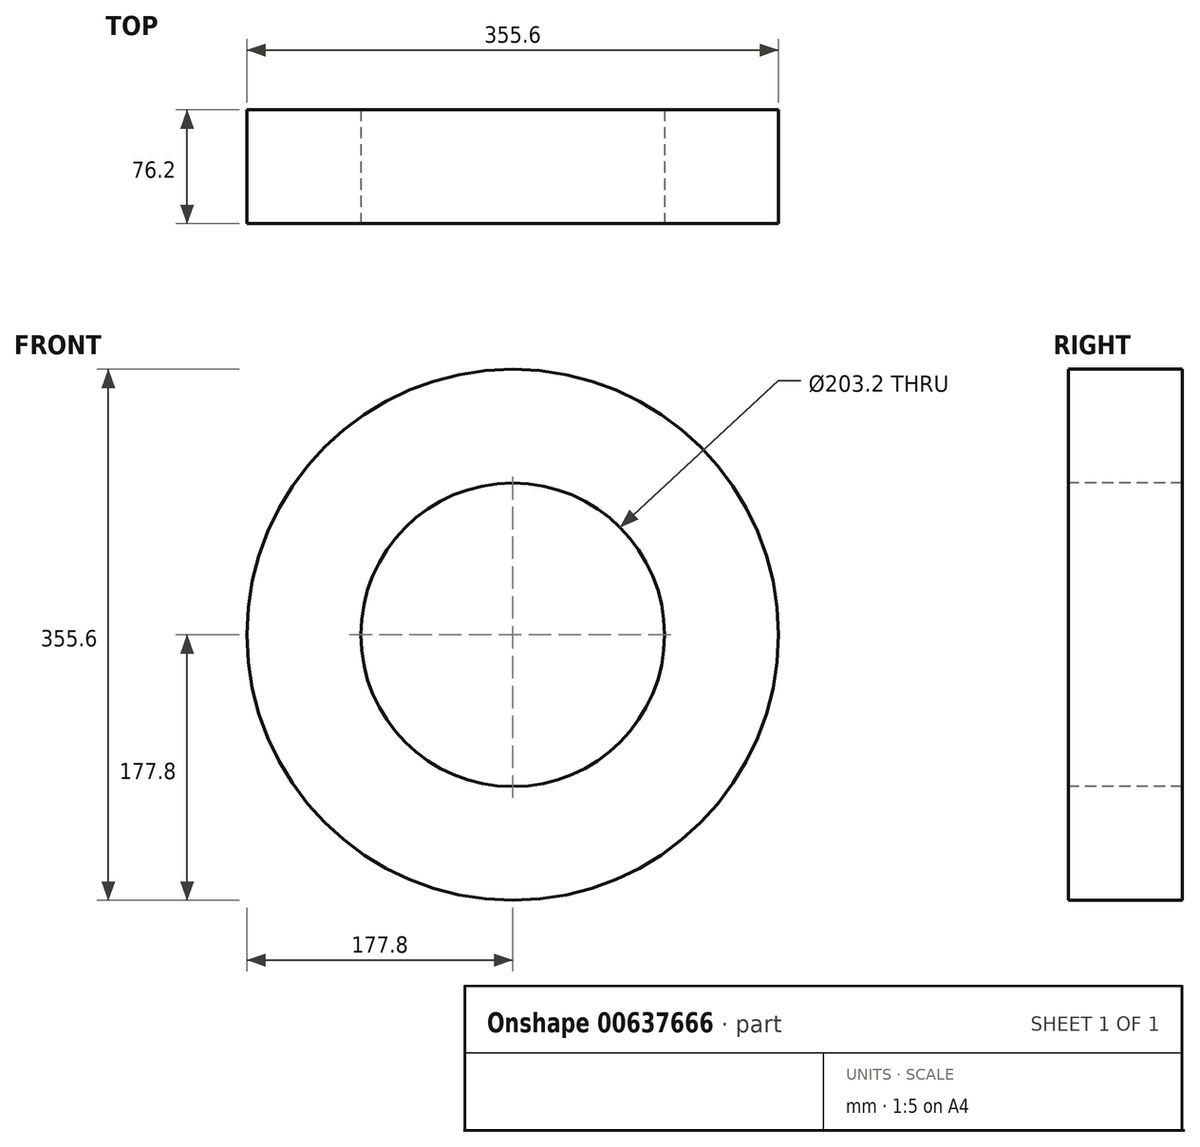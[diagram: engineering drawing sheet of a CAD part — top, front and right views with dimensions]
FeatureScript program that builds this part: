
annotation { "Feature Type Name" : "Feature", "Feature Type Description" : "" }
export const myFeature = defineFeature(function(context is Context, id is Id, definition is map)
    precondition{}
    {
        {
            var Q0;
            Q0=qCreatedBy(makeId("Top.planeOp"),FACE);
            var sketch = newSketch(context, id + "F0", { "sketchPlane" : qUnion([Q0])});
            skLineSegment(sketch, "E0.bottom", {"start": v(101.6, 0) * mm, "end": v(177.8, 0) * mm});
            skLineSegment(sketch, "E0.top", {"start": v(101.6, 76.2) * mm, "end": v(177.8, 76.2) * mm});
            skLineSegment(sketch, "E0.left", {"start": v(101.6, 0) * mm, "end": v(101.6, 76.2) * mm});
            skLineSegment(sketch, "E0.right", {"start": v(177.8, 0) * mm, "end": v(177.8, 76.2) * mm});
            skLineSegment(sketch, "E1", {"start": v(0, 0) * mm, "end": v(0, 84.62) * mm, "construction": true});
            skSolve(sketch);
        }
        {
            var Q0;
            Q0=makeQuery(id+"F0.imprint","IMPRINT",FACE,{"disambiguationData":[TD([[makeQuery(id+"F0.imprint","IMPRINT",EDGE,{"derivedFrom":sQuery(id+"F0.wireOp",EDGE,"E0.bottom")}),1.0]])]});
            var Q1;
            Q1=sQuery(id+"F0.wireOp",EDGE,"E1");
            revolve(context, id + "F1", {"entities" : qUnion([Q0]), "axis" : qUnion([Q1]), "revolveType" : RevolveType.FULL});
        }
    });
